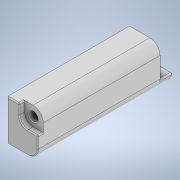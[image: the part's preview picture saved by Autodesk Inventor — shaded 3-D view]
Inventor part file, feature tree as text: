
AUTODESK INVENTOR PART (.ipt)
format: ipt  version: 2022 (Build 260153000, 153)  size: 196,608 bytes
history: native  units: mm
features: fillet x5, sketch x5, extrude x4, chamfer x2, hole x1
ambient origin geometry x8: Origin, YZ Plane, XZ Plane, XY Plane, X Axis, Y Axis, Z Axis, Center Point
bodies: Solid1 (feature_tree)
feature tree (17):
  extrude  "Extrusion1"  Depth=25.4mm
  extrude  "Extrusion2"  Depth=11.621mm
  extrude  "Extrusion3"  Depth=3.429mm TaperAngle=0.0deg
  hole  "Hole1"  [1 undecoded]
  fillet  "Fillet1"  Radius=7.938mm
  fillet  "Fillet2"  Radius=6.35mm
  fillet  "Fillet3"  Radius=6.35mm
  fillet  "Fillet4"  Radius=6.35mm
  chamfer  "Chamfer1"  Distance=0.794mm
  extrude  "Extrusion4"  Depth=5.271mm
  fillet  "Fillet5"  Radius=13.208mm
  chamfer  "Chamfer2"  Distance=0.6mm Angle=45.0deg
  sketch  "Sketch1"  dims[d0=25.4mm d1=25.4mm]
  sketch  "Sketch2"  dims[d2=84.138mm d3=0.0mm d4=11.621mm]
  sketch  "Sketch3"  dims[d5=11.621mm d6=3.429mm d7=0.0mm]
  sketch  "Sketch4"  dims[d8=19.558mm d9=19.558mm d10=7.938mm d11=0.0mm d12=6.35mm d13=6.35mm]
  sketch  "Sketch5"  dims[d14=5.334mm d15=6.0mm d16=9.779mm d17=2.0mm d18=14.3117mm d19=8.0mm d20=20.594885mm d21=6.35mm d22=0.794mm d23=5.271mm d24=13.208mm d25=0.6mm d26=2.0mm d27=45.0deg d28=25.4mm d29=6.35mm d30=84.138mm d31=0.0mm d32=0.794mm d33=0.6mm d34=2.0mm d35=45.0deg]
note: 1 required parameter value undecoded (feature->parameter linkage not recoverable at this tier; creation-order binding heuristic only, values carry confidence <= 0.55)
